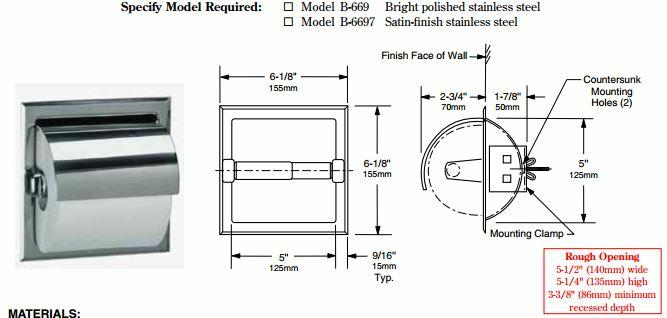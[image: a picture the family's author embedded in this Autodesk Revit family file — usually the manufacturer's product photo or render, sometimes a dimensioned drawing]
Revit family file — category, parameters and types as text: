
# Revit family: rba-bim-B6977
name_source: partatom
category: Plumbing Fixtures
revit_build: Autodesk Revit 2018 (Build: 20170223_1515(x64)
units: mm (PartAtom-declared; Revit-internal decimal feet)

## family parameters
Always vertical = No
Cut with Voids When Loaded = No
Part Type = Normal
Room Calculation Point = No
Round Connector Dimension = Use Diameter
Shared = Yes
Work Plane-Based = Yes

## types (1)
- B-6977
    CW Connection = No
    Default Elevation = 0 mm  [stored 0 ft]
    Description = Recessed Dual Toilet Roll Holder
    HW Connection = No
    Manufacturer = Bobrick Washroom Equipment
    Materials and Finishes = Satin Stainless Steel
    Model = B6977
    Modified Issue = 20201028.01
    Product URL = http://www.bobrick.com
    Revised Date = 23/08/2013
    URL = www.rba.com.au
    Vent Connection = No
    Waste Connection = No

note: [stored X ft] marks values corroborated as IEEE doubles in the binary element streams (Revit-internal decimal feet)

## geometry (parser evidence)
native form markers: Blend x2, Sweep x2
no freeform markers — native parametric forms only
